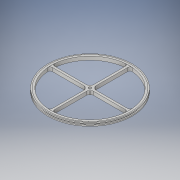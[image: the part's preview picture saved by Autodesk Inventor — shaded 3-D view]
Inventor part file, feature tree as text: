
AUTODESK INVENTOR PART (.ipt)
format: ipt  version: 2018 (Build 220112000, 112)  size: 430,080 bytes
history: native  units: in
note: dims shown in document units (in); Inventor stores cm internally (conversion verified against a paired STEP export)
features: extrude x8, sketch x8, fillet x2
ambient origin geometry x8: Origin, YZ Plane, XZ Plane, XY Plane, X Axis, Y Axis, Z Axis, Center Point
bodies: Solid1 (feature_tree)
feature tree (18):
  extrude  "Extrusion1"  Depth=4.849in
  extrude  "Extrusion2"  Depth=0.0625in
  extrude  "Extrusion3"  Depth=0.0625in TaperAngle=0.0deg
  extrude  "Extrusion4"  Depth=0.204in
  extrude  "Extrusion5"  Depth=0.204in
  extrude  "Extrusion6"  Depth=0.125in
  extrude  "Extrusion7"  Depth=0.204in TaperAngle=0.0deg
  fillet  "Fillet1"  Radius=0.125in
  fillet  "Fillet2"  Radius=0.125in
  extrude  "Extrusion8"  [1 undecoded]
  sketch  "Sketch1"  dims[d0=4.7244in d1=4.849in]
  sketch  "Sketch2"  dims[d2=0.0625in d3=0.0in d4=4.5in]
  sketch  "Sketch3"  dims[d5=0.0787in d6=0.0in d7=0.0625in d8=0.0in]
  sketch  "Sketch4"  dims[d9=0.204in d10=0.0in d11=4.5in]
  sketch  "Sketch5"  dims[d12=0.204in d13=0.0in d14=0.195in]
  sketch  "Sketch6"  dims[d15=0.204in d16=0.0in d17=0.125in]
  sketch  "Sketch7"  dims[d18=0.125in d19=0.204in d20=0.0in d21=0.125in d22=0.125in]
  sketch  "Sketch8"  dims[d23=0.204in d24=0.0in]
note: 1 required parameter value undecoded (feature->parameter linkage not recoverable at this tier; creation-order binding heuristic only, values carry confidence <= 0.55)
